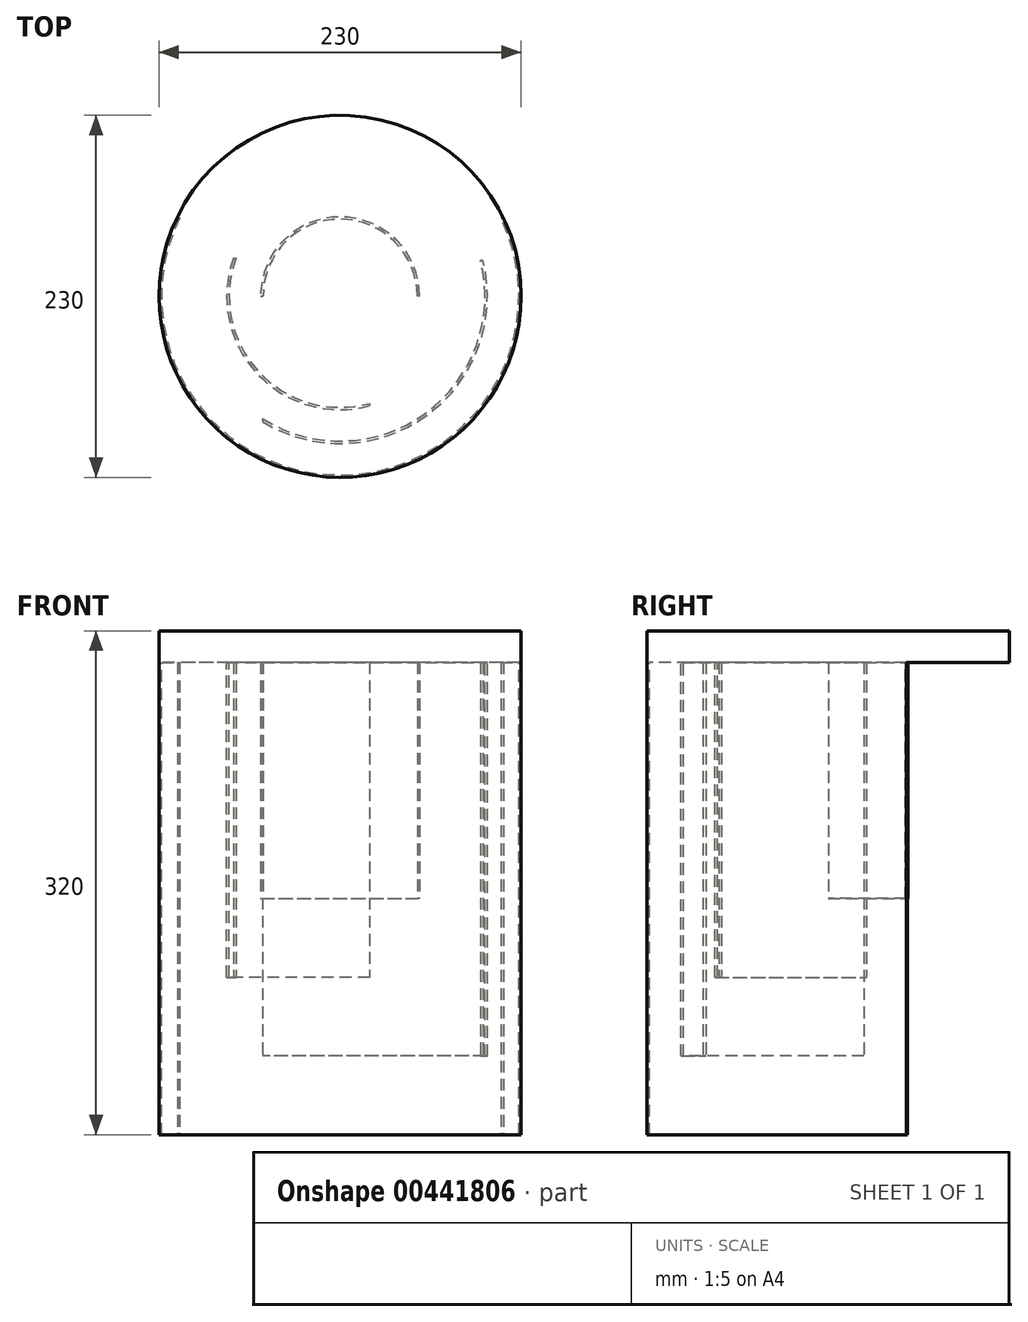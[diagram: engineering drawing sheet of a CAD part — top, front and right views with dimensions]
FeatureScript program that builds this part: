
annotation { "Feature Type Name" : "Feature", "Feature Type Description" : "" }
export const myFeature = defineFeature(function(context is Context, id is Id, definition is map)
    precondition{}
    {
        {
            var Q0;
            Q0=qCreatedBy(makeId("Top.planeOp"),FACE);
            var sketch = newSketch(context, id + "F0", { "sketchPlane" : qUnion([Q0])});
            skCircle(sketch, "E0", {"center": v(0, 0) * mm, "radius": 115 * mm});
            skSolve(sketch);
        }
        {
            var Q0;
            Q0=makeQuery(id+"F0.imprint","IMPRINT",FACE,{"disambiguationData":[TD([[makeQuery(id+"F0.imprint","IMPRINT",EDGE,{"derivedFrom":sQuery(id+"F0.wireOp",EDGE,"E0")}),1.0]])]});
            extrude(context, id + "F1", {"entities" : qUnion([Q0]), "depth" : 20 * mm});
        }
        {
            var Q0;
            Q0=makeQuery(id+"F1.opExtrude","CAP_FACE",FACE,{"disambiguationData":[OSD([sQuery(id+"F0.wireOp",EDGE,"E0")])],"isStart":true});
            var sketch = newSketch(context, id + "F2", { "sketchPlane" : qUnion([Q0])});
            skCircle(sketch, "E1", {"center": v(0, 0) * mm, "radius": 115 * mm});
            skCircle(sketch, "E2", {"center": v(0, 0) * mm, "radius": 113.5 * mm});
            skSolve(sketch);
        }
        {
            var Q0;
            Q0 = qSketchRegion(id + "F2", true);
            extrude(context, id + "F3", {"entities" : qUnion([Q0]), "operationType" : NewBodyOperationType.ADD, "depth" : 300 * mm, "offsetDistance" : 25 * mm});
        }
        {
            var Q0;
            Q0=makeQuery(id+"F2woZXPj5OQiuo1_1.boolean.opBoolean","SPLIT",FACE,{"disambiguationData":[TD([makeQuery(id+"F3.opExtrude","SWEPT_FACE",FACE,{"disambiguationData":[OSD([sQuery(id+"F2.wireOp",EDGE,"E2")])]})])],"derivedFrom":makeQuery(id+"F1.opExtrude","CAP_FACE",FACE,{"disambiguationData":[OSD([sQuery(id+"F0.wireOp",EDGE,"E0")])],"isStart":true})});
            var sketch = newSketch(context, id + "F4", { "sketchPlane" : qUnion([Q0])});
            skCircle(sketch, "E3", {"center": v(0, 0) * mm, "radius": 72 * mm});
            skCircle(sketch, "E4", {"center": v(0, 0) * mm, "radius": 70.5 * mm});
            skSolve(sketch);
        }
        {
            var Q0;
            Q0 = qSketchRegion(id + "F4", true);
            extrude(context, id + "F5", {"entities" : qUnion([Q0]), "operationType" : NewBodyOperationType.ADD, "depth" : 200 * mm});
        }
        {
            var Q0;
            Q0=makeQuery(id+"F5.boolean.opBoolean","SPLIT",FACE,{"disambiguationData":[TD([makeQuery(id+"F5.opExtrude","SWEPT_FACE",FACE,{"disambiguationData":[OSD([sQuery(id+"F4.wireOp",EDGE,"E4")])]})])],"derivedFrom":makeQuery(id+"F2woZXPj5OQiuo1_1.boolean.opBoolean","SPLIT",FACE,{"disambiguationData":[TD([makeQuery(id+"F2woZXPj5OQiuo1_1.opExtrude","SWEPT_FACE",FACE,{"disambiguationData":[OSD([sQuery(id+"FDGueIww0Ypvuo0_1.wireOp",EDGE,"JaUsiSq3-fuOc-w5x5-9ZTb-7nvuGy0SD6GS")])]})])],"derivedFrom":makeQuery(id+"F1.opExtrude","CAP_FACE",FACE,{"disambiguationData":[OSD([sQuery(id+"F0.wireOp",EDGE,"E0")])],"isStart":true})})});
            var sketch = newSketch(context, id + "F6", { "sketchPlane" : qUnion([Q0])});
            skCircle(sketch, "E5", {"center": v(0, 0) * mm, "radius": 50.5 * mm});
            skCircle(sketch, "E6", {"center": v(0, 0) * mm, "radius": 49 * mm});
            skSolve(sketch);
        }
        {
            var Q0;
            Q0 = qSketchRegion(id + "F6", true);
            extrude(context, id + "F7", {"entities" : qUnion([Q0]), "operationType" : NewBodyOperationType.ADD, "depth" : 150 * mm, "offsetDistance" : 25 * mm});
        }
        {
            var Q0;
            Q0=makeQuery(id+"F5.boolean.opBoolean","SPLIT",FACE,{"disambiguationData":[TD([makeQuery(id+"F3.opExtrude","SWEPT_FACE",FACE,{"disambiguationData":[OSD([sQuery(id+"F2.wireOp",EDGE,"E2")])]})])],"derivedFrom":makeQuery(id+"F1.opExtrude","CAP_FACE",FACE,{"disambiguationData":[OSD([sQuery(id+"F0.wireOp",EDGE,"E0")])],"isStart":true})});
            var sketch = newSketch(context, id + "F8", { "sketchPlane" : qUnion([Q0])});
            skCircle(sketch, "E7", {"center": v(0, 0) * mm, "radius": 93.5 * mm});
            skCircle(sketch, "E8", {"center": v(0, 0) * mm, "radius": 92 * mm});
            skSolve(sketch);
        }
        {
            var Q0;
            Q0 = qSketchRegion(id + "F8", true);
            extrude(context, id + "F9", {"entities" : qUnion([Q0]), "operationType" : NewBodyOperationType.ADD, "depth" : 250 * mm});
        }
        {
            var Q0;
            Q0=makeQuery(id+"F3.opExtrude","CAP_FACE",FACE,{"disambiguationData":[OSD([sQuery(id+"F2.wireOp",EDGE,"E1"),sQuery(id+"F2.wireOp",EDGE,"E2")])],"isStart":false});
            var sketch = newSketch(context, id + "F10", { "sketchPlane" : qUnion([Q0])});
            skLineSegment(sketch, "E9", {"start": v(-103.4, -50.35) * mm, "end": v(-102.1, -49.57) * mm});
            skLineSegment(sketch, "E10", {"start": v(102.1, -49.57) * mm, "end": v(103.77, -49.57) * mm});
            skSolve(sketch);
        }
        {
            var Q0;
            {var subQ0=sQuery(id+"F10.wireOp",EDGE,"E9");Q0=makeQuery(id+"F10.imprint","IMPRINT",FACE,{"disambiguationData":[TD([[makeQuery(id+"F10.imprint","IMPRINT",EDGE,{"derivedFrom":subQ0}),-1.0]])]});}
            extrude(context, id + "F11", {"entities" : qUnion([Q0]), "operationType" : NewBodyOperationType.REMOVE, "oppositeDirection" : true, "depth" : 300 * mm});
        }
        {
            var Q0;
            Q0=makeQuery(id+"F9.opExtrude","CAP_FACE",FACE,{"disambiguationData":[OSD([sQuery(id+"F8.wireOp",EDGE,"E7"),sQuery(id+"F8.wireOp",EDGE,"E8")])],"isStart":false});
            var sketch = newSketch(context, id + "F12", { "sketchPlane" : qUnion([Q0])});
            skLineSegment(sketch, "E11", {"start": v(90.7, -22.71) * mm, "end": v(89.15, -22.71) * mm});
            skLineSegment(sketch, "E12", {"start": v(-49.35, 77.65) * mm, "end": v(-49.35, 79.42) * mm});
            skSolve(sketch);
        }
        {
            var Q0;
            {var subQ0=sQuery(id+"F12.wireOp",EDGE,"E11");Q0=makeQuery(id+"F12.imprint","IMPRINT",FACE,{"disambiguationData":[TD([[makeQuery(id+"F12.imprint","IMPRINT",EDGE,{"derivedFrom":subQ0}),1.0]])]});}
            extrude(context, id + "F13", {"entities" : qUnion([Q0]), "operationType" : NewBodyOperationType.REMOVE, "oppositeDirection" : true, "depth" : 250 * mm});
        }
        {
            var Q0;
            Q0=makeQuery(id+"F5.opExtrude","CAP_FACE",FACE,{"disambiguationData":[OSD([sQuery(id+"F4.wireOp",EDGE,"E3"),sQuery(id+"F4.wireOp",EDGE,"E4")])],"isStart":false});
            var sketch = newSketch(context, id + "F14", { "sketchPlane" : qUnion([Q0])});
            skLineSegment(sketch, "E13", {"start": v(-67.77, -24.32) * mm, "end": v(-66.17, -24.32) * mm});
            skLineSegment(sketch, "E14", {"start": v(18.74, 67.96) * mm, "end": v(18.74, 69.52) * mm});
            skSolve(sketch);
        }
        {
            var Q0;
            {var subQ0=sQuery(id+"F14.wireOp",EDGE,"E13");Q0=makeQuery(id+"F14.imprint","IMPRINT",FACE,{"disambiguationData":[TD([[makeQuery(id+"F14.imprint","IMPRINT",EDGE,{"derivedFrom":subQ0}),-1.0]])]});}
            extrude(context, id + "F15", {"entities" : qUnion([Q0]), "operationType" : NewBodyOperationType.REMOVE, "oppositeDirection" : true, "depth" : 200 * mm});
        }
        {
            var Q0;
            Q0=makeQuery(id+"F7.opExtrude","CAP_FACE",FACE,{"disambiguationData":[OSD([sQuery(id+"F6.wireOp",EDGE,"E5"),sQuery(id+"F6.wireOp",EDGE,"E6")])],"isStart":false});
            var sketch = newSketch(context, id + "F16", { "sketchPlane" : qUnion([Q0])});
            skLineSegment(sketch, "E15", {"start": v(-50.5, 0) * mm, "end": v(-49, 0) * mm});
            skLineSegment(sketch, "E16", {"start": v(50.5, 0) * mm, "end": v(49, 0) * mm});
            skSolve(sketch);
        }
        {
            var Q0;
            {var subQ0=sQuery(id+"F16.wireOp",EDGE,"E15");Q0=makeQuery(id+"F16.imprint","IMPRINT",FACE,{"disambiguationData":[TD([[makeQuery(id+"F16.imprint","IMPRINT",EDGE,{"derivedFrom":subQ0}),1.0]])]});}
            extrude(context, id + "F17", {"entities" : qUnion([Q0]), "operationType" : NewBodyOperationType.REMOVE, "oppositeDirection" : true, "depth" : 150 * mm});
        }
        {
            var Q0;
            Q0=makeQuery(id+"F1.opExtrude","CAP_FACE",FACE,{"disambiguationData":[OSD([sQuery(id+"F0.wireOp",EDGE,"E0")])],"isStart":false});
            cPlane(context, id + "F18", {"entities" : qUnion([Q0]), "cplaneType" : CPlaneType.OFFSET, "offset" : 25 * mm, "width" : 150 * mm, "height" : 150 * mm});
        }
    });
